# Revit family: 3f_filippi_-_3f_diagon_soft_ugr_3f_filippi_-_23814_-_3f_diagon_25w-840_dali_soft_ugr_596x596
name_source: partatom
category: Lighting Fixtures
units: mm (PartAtom-declared; Revit-internal decimal feet)

## family parameters
Cut with Voids When Loaded = No
Host = Face
Light Source = No
Part Type = Normal
Room Calculation Point = No
Round Connector Dimension = Use Diameter
Shared = No

## types (1)
- 3F Filippi - 3F Dìagon Soft UGR (1 x LED, 3679 lm, 28 W, 4000 K)
    Apparent Load = 28 VA
    Approval mark = CE
    CIE Flux Codes = 59 92 100 100 100
    Color Rendering = 80
    Color Temperature = 4000 K
    Control Gear = Electronic transformer
    Default Elevation = 1800 mm
    Description = ILLUMINOTECHNICAL
Luminous efficiency 100% (DLOR 100%, ULOR 0%).
Initial luminous flux of the luminaire 3679 lm.
Direct symmetric distribution.
Installation Interdistance Transv.D = 1.23 x hu - Long.D = 1.23 x hu.
Average luminance <3000 cd/m² for radial angles >65°.
Tabular UGR (CIE 117 - 4H-8H; S=0.25H; 70/50/20): RUG 18.7 - 18.7.
Beam angle: 102° - 101°.
Luminous efficacy 131 lm/W.
Lifetime (L95/B10): 30000 h. (tq+25°C)
Lifetime (L90/B10): 50000 h. (tq+25°C)
Lifetime (L80/B10): 80000 h. (tq+25°C)
Lifetime (L75/B10): 100000 h. (tq+25°C)
Sudden decreased luminous flux after 50000 hours: 0% (C0).
Photobiological safety in compliance with IEC/TR 62778: RG0 risk exempt, (IEC 62471).
In compliance with IEC/EN 62722-2-1 - IEC/EN 62717 standards.

SOURCE
Squared LED module 25W/840.
Energy efficiency class (UE 2019/2020 - UE 2019/2015): C.
CIE 13.3 Colour rendering index: CRI >80 (R9 <50%).
IES TM-30 Fidelity Index: Rf = 84 Rg = 95.
CCT nominal colour temperature 4000 K.
Colour initial tolerance (MacAdam): SDCM 3.

MECHANICAL
Housing in hot-galvanised steel, painted in white polyester.
Honeycombed diagonal screen in white anti-glare polycarbonate.
Opal methacrylate (PMMA) rhomboid lenses with differentiated, engraved and prismatic surfaces for diffused, soft lighting and excellent visual comfort.
Luminaire with limited surface temperature. - D - (EN 60598-2-24)
Dimensions: 596x596 mm, height 30 mm. Weight 3.75 kg.
IP43 protection degree for exposed part, IP20 for recessed part.
Mechanical strength to impacts IK06 (1 joule).
Glow-wire test resistance 650°C.

ELECTRICAL
Halogen Free DALI-2, PUSH-DIM, electronic wiring 230V-50/60Hz, power factor 0.95 at full load, THD <25%, constant output current, class I, 1 driver, 1 DALI addresse.
Power of the luminaire 28 W.
ENEC - CE.
SAFE FLICKER: PstLM=<1 and SVM=<0.4 (IEC TR 61547-1 and IEC TR 63158), to ensure a more comfortable and safe light.
Luminaire compliant with EN 60598-2-22 for power supply from a centralised emergency system CPSS (Central Power Supply System), not incorporated in the luminaire - high risk areas excluded. The default power and flux are 100% in AC and 15% in DC.
Ambient temperature from 0°C to +25°C.
Temperature class T6 max 85°C.
Quick connection.
Relative humidity UR: <85%.

INSTALLATION
Lay-in recessed fitting.
Height only 30 mm.
Installation in false ceilings with exposed structure.
Installation after mounting the false ceiling, resting on the exposed structure, minimum void of 140 mm from the lower edge of the structure.
Simultaneous installation with the false ceiling, minimum void of 60 mm from the lower edge of the structure.
All accessories dedicated to this product are available on the Catalog and on our website www.3F-Filippi.com.

APPLICATIONS
Environments: staterooms, with VDTs, offices.
Environments with exacting visual tasks, where diffused soft light for optimum visual comfort is required.

LIGHT MANAGEMENT
Recommended minimum setting: 10%.
The device, equipped with DALI-2 driver, can be controlled manually with 3F Easy Dim technology or automatically/manually with 3F Smart Dimming technology and/or centralised DALI systems.
DALI-2 certification guarantees interoperability with other devices with the same certification.
In electrical systems without a regulation system (manual or automatic) and DALI bus, a suitable jumper must be made on the DA-DA terminals of the appliance.

WARNING
Luminaire designed for disposal/recycling at end-of-life.
Replaceable (LED only) light source by a professional. Replaceable control gear by a professional.
    Height = 0 mm  [stored 0 ft]
    Lamp = 1 x LED
    Lamp Light Flux = 3679 lm
    Lamp Power = 28 W
    Lamp count = 1
    Length = 596 mm
    Lifetime = 50000 h
    Luminous efficacy = 131 lm/W
    Manufacturer = 3F Filippi
    ModVariant = No
    Model = 3F Filippi - 23814 - 3F Diagon 25W-840 DALI SOFT UGR 596x596
    Mounting Place = Ceiling
    Mounting Type = Recessed
    Number of Poles = 1
    OnlyDefault = Yes
    Power Factor = 1
    Product Name = 3F Filippi - 3F Dìagon Soft UGR
    Product group = recessed luminaire
    ProductGroupID = 4
    Protection Class = Protection class I
    Protection Degree = IP 20
    RLX_Detail_Level = 1
    RLX_Emergency_Light_Flux = 0 lm
    RLX_Emergency_Type = 0
    RLX_Emergency_Type_DB = No
    RlxData = <blob elided: 80597 chars, md5=53951859>
    Socket = socket
    Standby Power = 0 W
    System Light Flux = 3679 lm
    System Power = 28 W
    Type Comments = Product without accessories
    Type Image = 3ffilippi_3f_diagon_soft_ugr.jpg
    URL = http://relux.com
    VarID = ---
    Voltage = 0 V
    Weight = 0.00 kg
    Width = 596 mm

note: [stored X ft] marks values corroborated as IEEE doubles in the binary element streams (Revit-internal decimal feet)

## geometry (parser evidence)
native form markers: Sweep x12
no freeform markers — native parametric forms only
